# Revit family: CY-956MH
name_source: partatom
category: Plumbing Fixtures
revit_build: Autodesk Revit Architecture 2012 (Build: 20110309_2315(x64)
units: mm (PartAtom-declared; Revit-internal decimal feet)

## types (1)
- CY-956MH
    Assembly Code = D2010
    CW Connection = Yes
    CWFU = 0
    Cartridge = S-SE950-1-F
    Cost = 0 $
    Default Elevation = 0' - 0"
    Description = Undertile mixer single lever. 2X1/2"FI, 1X1/2" + 1X3/4 female outlets
    HW Connection = Yes
    HWFU = 0
    Handle = S-CY950/1
    Keynote = * 2 x 1/2" female inlets, 1 x 1/2" shower outlet and 1 x 3/4" female bath outlet
    Manufacturer = COBRA
    Material = Chrome Polished
    Model = CY-956MH
    Range = Cyrano Minimalistic Handle
    Type Comments = SANS 1480
    URL = http://www.cobra.co.za
    Undertile face plate = S-CY961/2
    Vent Connection = No
    WFU = 0
    Waste Connection = No

## geometry (parser evidence)
native form markers: Blend x2
no freeform markers — native parametric forms only
